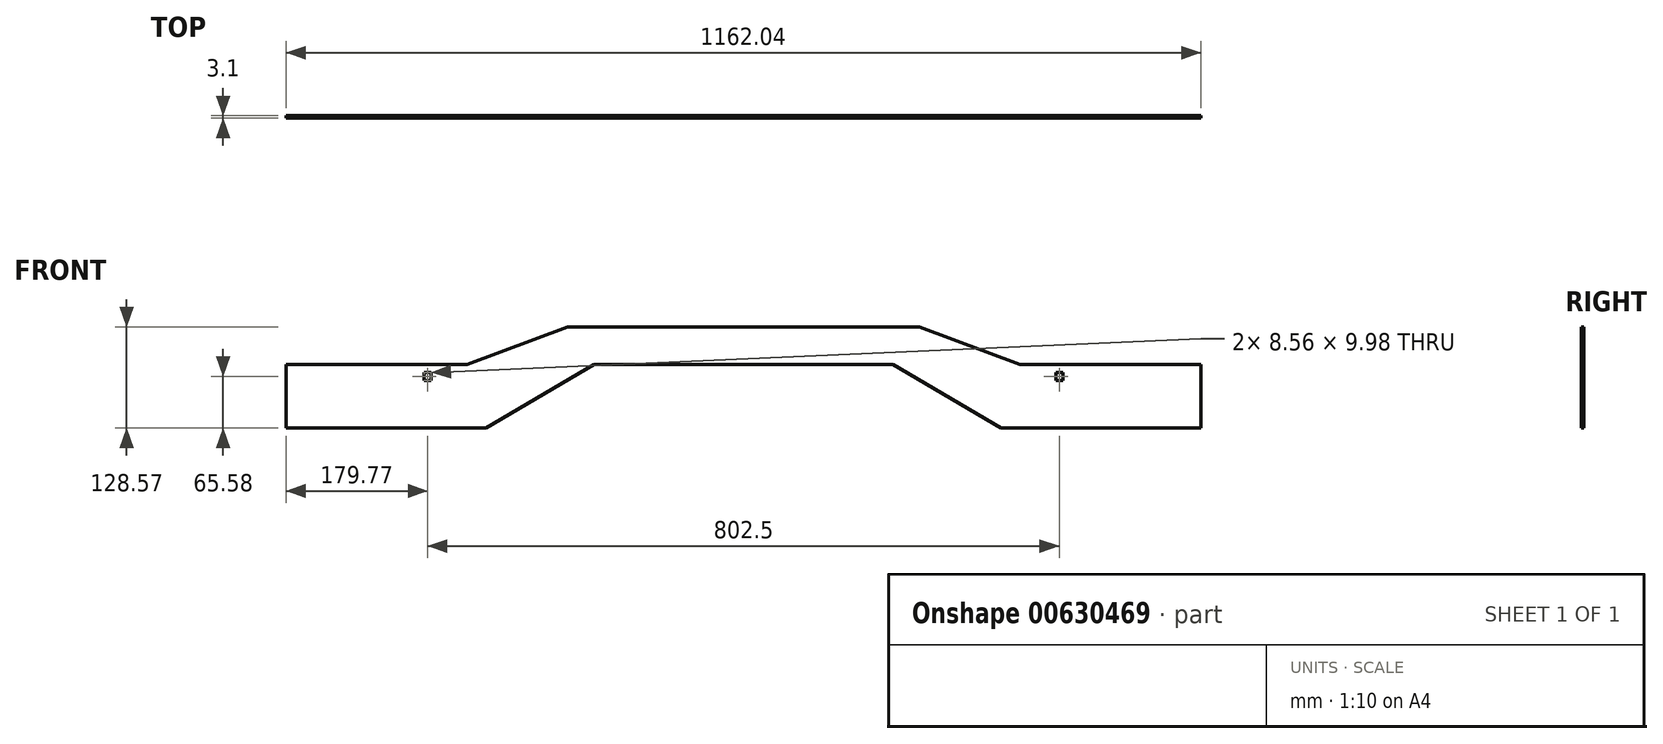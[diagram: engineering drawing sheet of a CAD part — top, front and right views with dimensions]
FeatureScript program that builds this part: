
annotation { "Feature Type Name" : "Feature", "Feature Type Description" : "" }
export const myFeature = defineFeature(function(context is Context, id is Id, definition is map)
    precondition{}
    {
        {
            var Q0;
            Q0=qCreatedBy(makeId("Front.planeOp"),FACE);
            var sketch = newSketch(context, id + "F0", { "sketchPlane" : qUnion([Q0])});
            skLineSegment(sketch, "E0", {"start": v(-581.02, -37.88) * mm, "end": v(-581.02, -118.85) * mm});
            skLineSegment(sketch, "E1", {"start": v(-581.02, -118.85) * mm, "end": v(-327.03, -118.85) * mm});
            skLineSegment(sketch, "E2", {"start": v(-327.03, -118.85) * mm, "end": v(-189.8, -37.9) * mm});
            skLineSegment(sketch, "E3", {"start": v(-189.8, -37.9) * mm, "end": v(0, -37.9) * mm});
            skLineSegment(sketch, "E4", {"start": v(-581.02, -37.88) * mm, "end": v(-351.03, -37.88) * mm});
            skLineSegment(sketch, "E5", {"start": v(-351.03, -37.88) * mm, "end": v(-223.57, 9.72) * mm});
            skLineSegment(sketch, "E6", {"start": v(-223.57, 9.72) * mm, "end": v(0, 9.72) * mm});
            skLineSegment(sketch, "E7", {"start": v(0, 9.72) * mm, "end": v(0, -37.9) * mm});
            skSolve(sketch);
        }
        {
            var Q0;
            Q0 = qSketchRegion(id + "F0", true);
            extrude(context, id + "F1", {"entities" : qUnion([Q0]), "depth" : 3.1 * mm, "offsetDistance" : 25 * mm});
        }
        {
            var Q0;
            Q0=makeQuery(id+"F1.opExtrude","SWEPT_BODY",BODY,{"disambiguationData":[OSD([sQuery(id+"F0.wireOp",EDGE,"E0"),sQuery(id+"F0.wireOp",EDGE,"E1"),sQuery(id+"F0.wireOp",EDGE,"E2"),sQuery(id+"F0.wireOp",EDGE,"E3"),sQuery(id+"F0.wireOp",EDGE,"E4"),sQuery(id+"F0.wireOp",EDGE,"E5"),sQuery(id+"F0.wireOp",EDGE,"E6"),sQuery(id+"F0.wireOp",EDGE,"E7")])]});
            var Q1;
            Q1=qCreatedBy(makeId("Right.planeOp"),FACE);
            mirror(context, id + "F2", {"operationType" : NewBodyOperationType.ADD, "entities" : qUnion([Q0]), "mirrorPlane" : qUnion([Q1])});
        }
        {
            var Q0;
            {var subQ0=makeQuery(id+"F1.opExtrude","CAP_FACE",FACE,{"disambiguationData":[OSD([sQuery(id+"F0.wireOp",EDGE,"E0"),sQuery(id+"F0.wireOp",EDGE,"E1"),sQuery(id+"F0.wireOp",EDGE,"E2"),sQuery(id+"F0.wireOp",EDGE,"E3"),sQuery(id+"F0.wireOp",EDGE,"E4"),sQuery(id+"F0.wireOp",EDGE,"E5"),sQuery(id+"F0.wireOp",EDGE,"E6"),sQuery(id+"F0.wireOp",EDGE,"E7")])],"isStart":false});Q0=makeQuery(id+"F2.boolean.opBoolean","MERGE",FACE,{"derivedFrom":[subQ0,makeQuery(id+"F2.opPattern","COPY",FACE,{"derivedFrom":subQ0,"instanceName":"1"})]});}
            var sketch = newSketch(context, id + "F3", { "sketchPlane" : qUnion([Q0])});
            skLineSegment(sketch, "E8.bottom", {"start": v(396.97, -48.28) * mm, "end": v(405.53, -48.28) * mm});
            skLineSegment(sketch, "E8.top", {"start": v(396.97, -58.26) * mm, "end": v(405.53, -58.26) * mm});
            skLineSegment(sketch, "E8.left", {"start": v(396.97, -48.28) * mm, "end": v(396.97, -58.26) * mm});
            skLineSegment(sketch, "E8.right", {"start": v(405.53, -48.28) * mm, "end": v(405.53, -58.26) * mm});
            skLineSegment(sketch, "E9.MirrorCS", {"start": v(-405.53, -48.28) * mm, "end": v(-405.53, -58.26) * mm});
            skLineSegment(sketch, "E10.MirrorCS", {"start": v(-396.97, -48.28) * mm, "end": v(-405.53, -48.28) * mm});
            skLineSegment(sketch, "E11.MirrorCS", {"start": v(-396.97, -58.26) * mm, "end": v(-405.53, -58.26) * mm});
            skLineSegment(sketch, "E12.MirrorCS", {"start": v(-396.97, -48.28) * mm, "end": v(-396.97, -58.26) * mm});
            skSolve(sketch);
        }
        {
            var Q0;
            Q0 = qSketchRegion(id + "F3", true);
            extrude(context, id + "F4", {"entities" : qUnion([Q0]), "operationType" : NewBodyOperationType.REMOVE, "oppositeDirection" : true, "depth" : 25.4 * mm, "offsetDistance" : 25.4 * mm});
        }
    });
